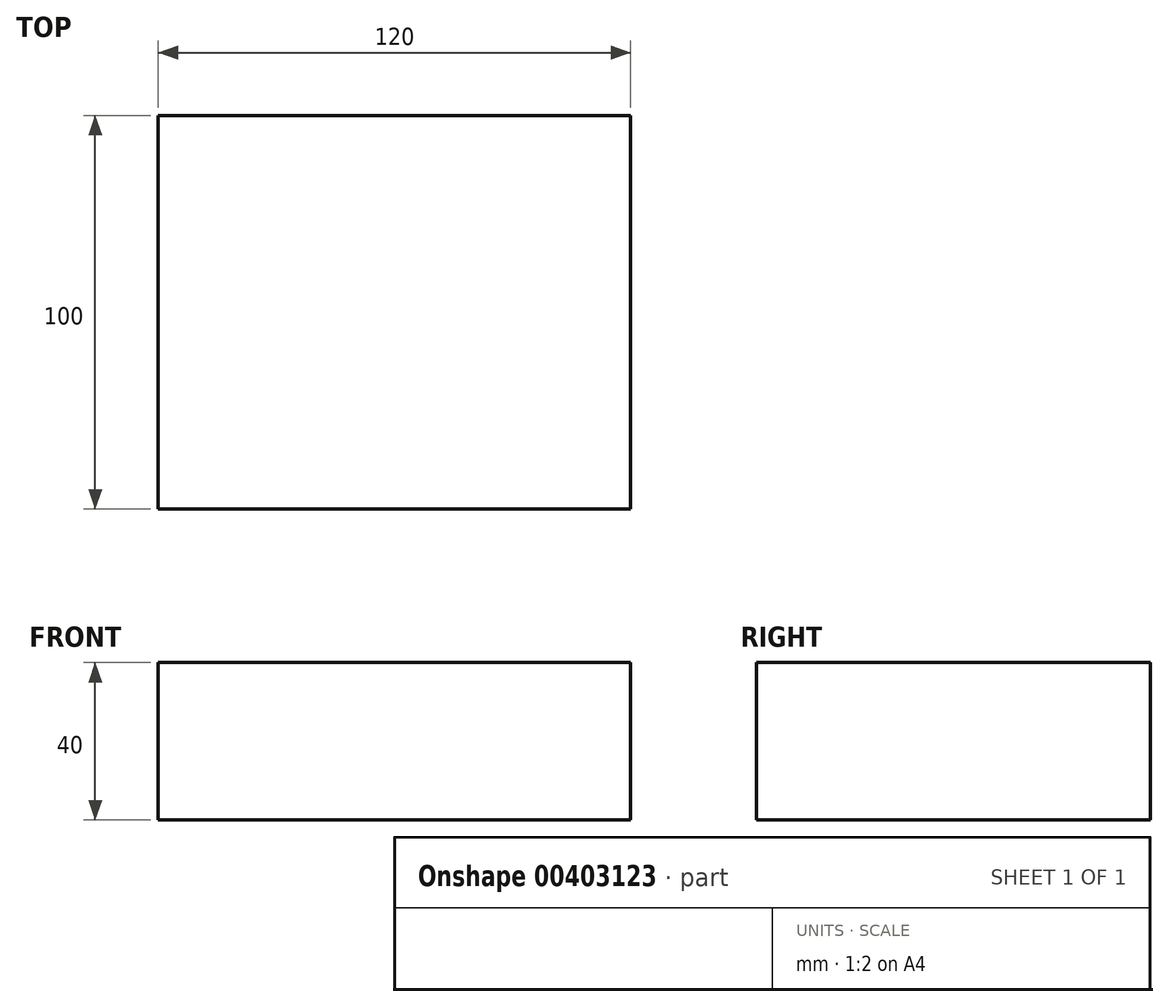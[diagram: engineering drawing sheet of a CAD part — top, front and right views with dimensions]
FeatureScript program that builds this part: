
annotation { "Feature Type Name" : "Feature", "Feature Type Description" : "" }
export const myFeature = defineFeature(function(context is Context, id is Id, definition is map)
    precondition{}
    {
        {
            var Q0;
            Q0=qCreatedBy(makeId("Top.planeOp"),FACE);
            var sketch = newSketch(context, id + "F0", { "sketchPlane" : qUnion([Q0])});
            skLineSegment(sketch, "E0.bottom", {"start": v(0, 0) * mm, "end": v(120, 0) * mm});
            skLineSegment(sketch, "E0.top", {"start": v(0, 100) * mm, "end": v(120, 100) * mm});
            skLineSegment(sketch, "E0.left", {"start": v(0, 0) * mm, "end": v(0, 100) * mm});
            skLineSegment(sketch, "E0.right", {"start": v(120, 0) * mm, "end": v(120, 100) * mm});
            skSolve(sketch);
        }
        {
            var Q0;
            Q0 = qSketchRegion(id + "F0", true);
            extrude(context, id + "F1", {"entities" : qUnion([Q0]), "depth" : 40 * mm});
        }
    });
